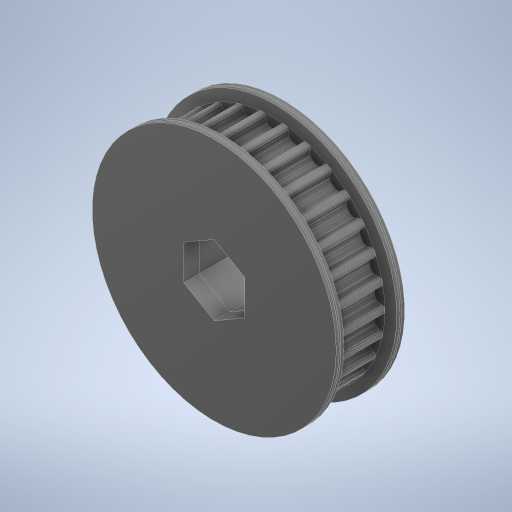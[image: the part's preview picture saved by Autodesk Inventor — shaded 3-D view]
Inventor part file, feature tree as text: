
AUTODESK INVENTOR PART (.ipt)
format: ipt  version: 2024 (Build 280153000, 153)  size: 1,356,288 bytes
history: native  units: in
note: dims shown in document units (in); Inventor stores cm internally (conversion verified against a paired STEP export)
features: extrude x6, sketch x6, mirror x2, plane x1, other x1
ambient origin geometry x8: Origin, YZ Plane, XZ Plane, XY Plane, X Axis, Y Axis, Z Axis, Center Point
bodies: Solid1 (feature_tree), Solid2 (feature_tree), Solid3 (feature_tree)
feature tree (16):
  plane  "Work Plane1"
  extrude  "Extrusion1"  Depth=0.0394in TaperAngle=0.0deg
  extrude  "Extrusion2"  Depth=0.0394in TaperAngle=0.0deg
  extrude  "Extrusion3"  TaperAngle=0.0deg  [1 undecoded]
  extrude  "Extrusion4"  [1 undecoded]
  extrude  "Extrusion5"  [1 undecoded]
  extrude  "Extrusion6"  [1 undecoded]
  sketch  "Sketch1"  dims[d0=0.1181in d1=0.0in d2=0.0394in d3=0.0in]
  sketch  "Sketch2"  dims[d4=0.0394in d5=0.0in d6=0.0394in d7=0.0in]
  sketch  "Sketch3"  dims[d8=0.505in d9=0.0in d10=0.0in]
  sketch  "Sketch4"  dims[d11=0.125in d12=0.0in]
  sketch  "Sketch5"
  sketch  "Sketch6"
  mirror  "Mirror1"
  mirror  "Mirror1:1"
  other  "Cut-Extrude6"
note: 4 required parameter values undecoded (feature->parameter linkage not recoverable at this tier; creation-order binding heuristic only, values carry confidence <= 0.55)
